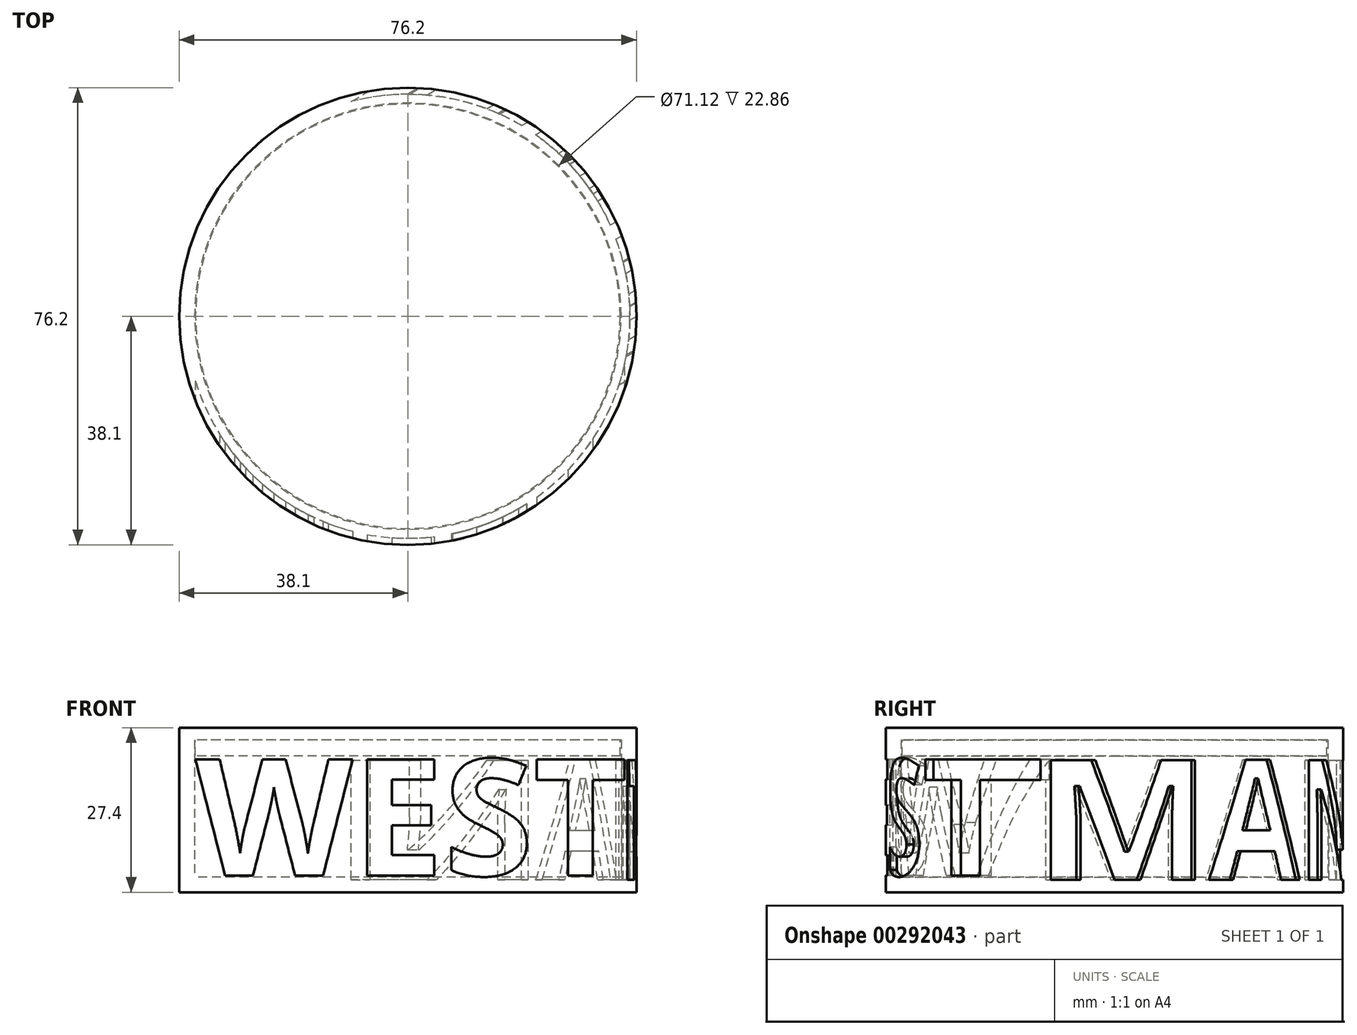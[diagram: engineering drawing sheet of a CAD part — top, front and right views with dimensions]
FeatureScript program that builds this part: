
annotation { "Feature Type Name" : "Feature", "Feature Type Description" : "" }
export const myFeature = defineFeature(function(context is Context, id is Id, definition is map)
    precondition{}
    {
        {
            var Q0;
            Q0=qCreatedBy(makeId("Top.planeOp"),FACE);
            var sketch = newSketch(context, id + "F0", { "sketchPlane" : qUnion([Q0])});
            skCircle(sketch, "E0", {"center": v(0, 0) * mm, "radius": 38.1 * mm});
            skSolve(sketch);
        }
        {
            var Q0;
            Q0 = qSketchRegion(id + "F0", true);
            extrude(context, id + "F1", {"entities" : qUnion([Q0]), "depth" : 25.4 * mm});
        }
        {
            var Q0;
            Q0=makeQuery(id+"F1.opExtrude","CAP_FACE",FACE,{"disambiguationData":[OSD([sQuery(id+"F0.wireOp",EDGE,"E0")])],"isStart":false});
            shell(context, id + "F2", {"entities" : qUnion([Q0]), "thickness" : 2.54 * mm});
        }
        {
            var Q0;
            Q0=makeQuery(id+"F1.opExtrude","CAP_FACE",FACE,{"disambiguationData":[OSD([sQuery(id+"F0.wireOp",EDGE,"E0")])],"isStart":false});
            var sketch = newSketch(context, id + "F3", { "sketchPlane" : qUnion([Q0])});
            skCircle(sketch, "E1.0", {"center": v(0, 0) * mm, "radius": 35.4 * mm});
            skCircle(sketch, "E2.0", {"center": v(0, 0) * mm, "radius": 38.1 * mm});
            skSolve(sketch);
        }
        {
            var Q0;
            Q0=makeQuery(id+"F3.imprint","IMPRINT",FACE,{"disambiguationData":[TD([[makeQuery(id+"F3.imprint","IMPRINT",EDGE,{"derivedFrom":sQuery(id+"F3.wireOp",EDGE,"E1.0")}),1.0]])]});
            extrude(context, id + "F4", {"entities" : qUnion([Q0]), "oppositeDirection" : true, "depth" : 2.7 * mm, "hasSecondDirection" : true, "secondDirectionOppositeDirection" : false, "secondDirectionDepth" : 2 * mm});
        }
        {
            var Q0;
            Q0=makeQuery(id+"F4.opExtrude","CAP_FACE",FACE,{"disambiguationData":[OSD([sQuery(id+"F3.wireOp",EDGE,"E1.0")])],"isStart":true});
            var sketch = newSketch(context, id + "F5", { "sketchPlane" : qUnion([Q0])});
            skCircle(sketch, "E3", {"center": v(0, 0) * mm, "radius": 38.1 * mm});
            skSolve(sketch);
        }
        {
            var Q0;
            Q0 = qSketchRegion(id + "F5", true);
            extrude(context, id + "F6", {"entities" : qUnion([Q0]), "operationType" : NewBodyOperationType.ADD, "oppositeDirection" : true, "depth" : 2 * mm});
        }
        {
            var Q0;
            Q0=qCreatedBy(makeId("Front.planeOp"),FACE);
            cPlane(context, id + "F7", {"entities" : qUnion([Q0]), "cplaneType" : CPlaneType.OFFSET, "offset" : 47.4 * mm, "width" : 150 * mm, "height" : 150 * mm});
        }
        {
            var Q0;
            Q0=qCreatedBy(makeId("Top.planeOp"),FACE);
            var sketch = newSketch(context, id + "F8", { "sketchPlane" : qUnion([Q0])});
            skCircle(sketch, "E4.0", {"center": v(0, 0) * mm, "radius": 37 * mm});
            skSolve(sketch);
        }
        {
            var Q0;
            Q0=sQuery(id+"F8.wireOp",EDGE,"E4.0");
            extrude(context, id + "F9", {"bodyType" : ToolBodyType.SURFACE, "surfaceEntities" : qUnion([Q0]), "depth" : 30 * mm});
        }
        {
            var Q0;
            Q0=qCreatedBy(id+"F7.planeOp",FACE);
            var sketch = newSketch(context, id + "F10", { "sketchPlane" : qUnion([Q0])});
            skText(sketch, "E5", { "text": "WEST", "fontName": "OpenSans-Bold.ttf"});
            const initialGuessF10  = {"E5": [-0.0354, 0.0028, 1, 0, 0.01951]};
            skSetInitialGuess(sketch, initialGuessF10);
            skSolve(sketch);
        }
        {
            var Q0;
            Q0 = qSketchRegion(id + "F10", true);
            var Q1;
            Q1=makeQuery(id+"F9.opExtrude","SWEPT_BODY",BODY,{"disambiguationData":[OSD([sQuery(id+"F8.wireOp",EDGE,"E4.0")])]});
            extrude(context, id + "F11", {"entities" : qUnion([Q0]), "operationType" : NewBodyOperationType.REMOVE, "endBound" : BoundingType.UP_TO_BODY, "oppositeDirection" : true, "endBoundEntityBody" : qUnion([Q1]), "depth" : 25 * mm});
        }
        {
            var Q0;
            Q0=qCreatedBy(makeId("Right.planeOp"),FACE);
            var sketch = newSketch(context, id + "F12", { "sketchPlane" : qUnion([Q0])});
            skLineSegment(sketch, "E6", {"start": v(0, 52.69) * mm, "end": v(0, -30.03) * mm, "construction": true});
            skSolve(sketch);
        }
        {
            var Q0;
            Q0=qCreatedBy(makeId("Right.planeOp"),FACE);
            var Q1;
            Q1=sQuery(id+"F12.wireOp",EDGE,"E6");
            cPlane(context, id + "F13", {"entities" : qUnion([Q0, Q1]), "cplaneType" : CPlaneType.LINE_ANGLE, "offset" : 25 * mm, "angle" : 330 * degree, "width" : 150 * mm, "height" : 150 * mm});
        }
        {
            var Q0;
            Q0=qCreatedBy(id+"F13.planeOp",FACE);
            cPlane(context, id + "F14", {"entities" : qUnion([Q0]), "cplaneType" : CPlaneType.OFFSET, "offset" : 57.4 * mm, "oppositeDirection" : true, "width" : 150 * mm, "height" : 150 * mm});
        }
        {
            var Q0;
            Q0=qCreatedBy(id+"F14.planeOp",FACE);
            var sketch = newSketch(context, id + "F15", { "sketchPlane" : qUnion([Q0])});
            skLineSegment(sketch, "E7.0", {"start": v(0, 52.69) * mm, "end": v(0, -30.03) * mm, "construction": true});
            skSolve(sketch);
        }
        {
            var Q0;
            Q0=qCreatedBy(id+"F14.planeOp",FACE);
            var Q1;
            Q1=sQuery(id+"F15.wireOp",EDGE,"E7.0");
            cPlane(context, id + "F16", {"entities" : qUnion([Q0, Q1]), "cplaneType" : CPlaneType.LINE_ANGLE, "offset" : 25 * mm, "angle" : 0 * degree, "width" : 150 * mm, "height" : 150 * mm});
        }
        {
            var Q0;
            Q0=qCreatedBy(id+"F16.planeOp",FACE);
            var sketch = newSketch(context, id + "F17", { "sketchPlane" : qUnion([Q0])});
            skText(sketch, "E8", { "text": "MAN", "fontName": "OpenSans-Bold.ttf"});
            const initialGuessF17  = {"E8": [-0.03, 0.00207, 1, 0, 0.02008]};
            skSetInitialGuess(sketch, initialGuessF17);
            skSolve(sketch);
        }
        {
            var Q0;
            Q0 = qSketchRegion(id + "F17", true);
            var Q1;
            Q1=makeQuery(id+"F9.opExtrude","SWEPT_BODY",BODY,{"disambiguationData":[OSD([sQuery(id+"F8.wireOp",EDGE,"E4.0")])]});
            extrude(context, id + "F18", {"entities" : qUnion([Q0]), "operationType" : NewBodyOperationType.REMOVE, "endBound" : BoundingType.UP_TO_BODY, "oppositeDirection" : true, "endBoundEntityBody" : qUnion([Q1]), "depth" : 25 * mm});
        }
        {
            var Q0;
            Q0=qCreatedBy(makeId("Right.planeOp"),FACE);
            var sketch = newSketch(context, id + "F19", { "sketchPlane" : qUnion([Q0])});
            skCircle(sketch, "E9", {"center": v(0, 26.49) * mm, "radius": 0.54 * mm});
            skSolve(sketch);
        }
        {
            var Q0;
            Q0 = qSketchRegion(id + "F19", true);
            extrude(context, id + "F20", {"entities" : qUnion([Q0]), "operationType" : NewBodyOperationType.ADD, "endBound" : BoundingType.SYMMETRIC, "depth" : 75.2 * mm});
        }
    });
